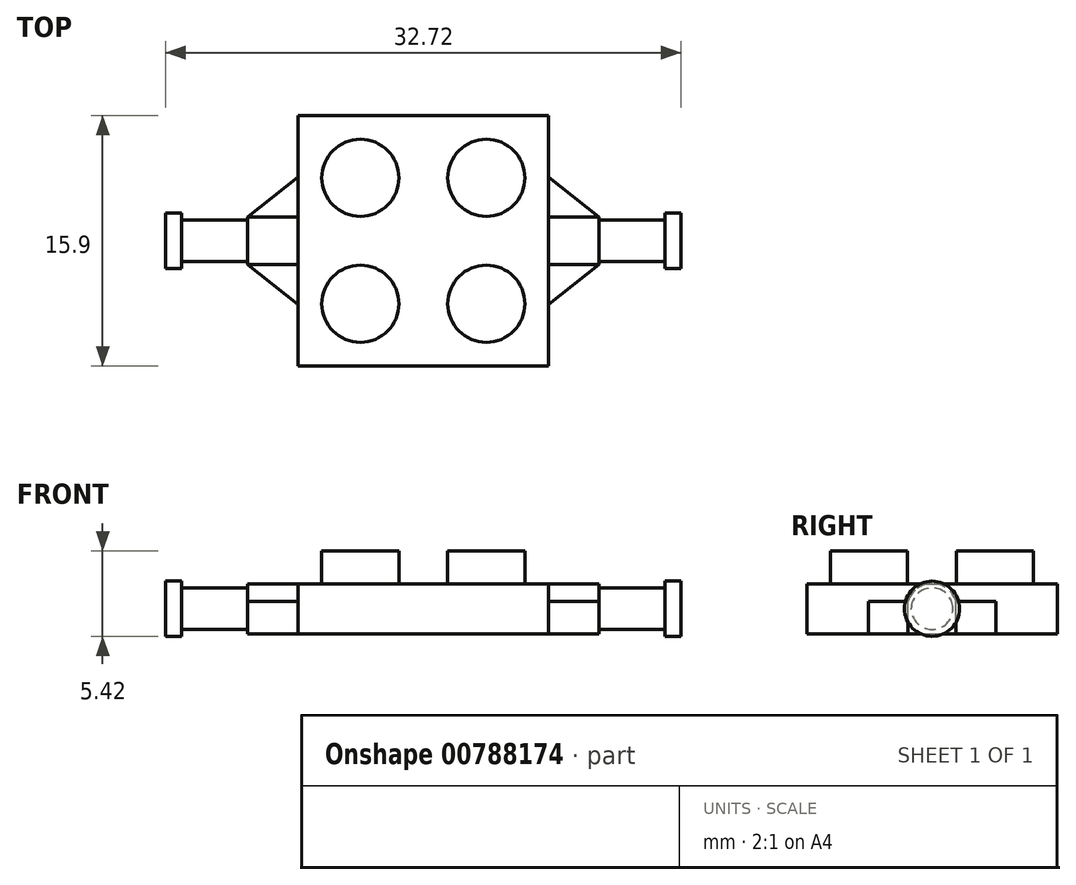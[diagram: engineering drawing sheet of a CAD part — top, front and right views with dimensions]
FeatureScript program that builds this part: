
annotation { "Feature Type Name" : "Feature", "Feature Type Description" : "" }
export const myFeature = defineFeature(function(context is Context, id is Id, definition is map)
    precondition{}
    {
        {
            var Q0;
            Q0=qCreatedBy(makeId("Top.planeOp"),FACE);
            var sketch = newSketch(context, id + "F0", { "sketchPlane" : qUnion([Q0])});
            skLineSegment(sketch, "E0.bottom", {"start": v(0, 0) * mm, "end": v(15.9, 0) * mm});
            skLineSegment(sketch, "E0.top", {"start": v(0, 15.9) * mm, "end": v(15.9, 15.9) * mm});
            skLineSegment(sketch, "E0.left", {"start": v(0, 0) * mm, "end": v(0, 15.9) * mm});
            skLineSegment(sketch, "E0.right", {"start": v(15.9, 0) * mm, "end": v(15.9, 15.9) * mm});
            skSolve(sketch);
        }
        {
            var Q0;
            Q0=qSketchRegion(id+"F0",true);
            extrude(context, id + "F1", {"entities" : qUnion([Q0]), "depth" : 3.18 * mm, "offsetDistance" : 25 * mm});
        }
        {
            var Q0;
            Q0=makeQuery(id+"F1.opExtrude","CAP_FACE",FACE,{"disambiguationData":[OSD([sQuery(id+"F0.wireOp",EDGE,"E0.bottom"),sQuery(id+"F0.wireOp",EDGE,"E0.top"),sQuery(id+"F0.wireOp",EDGE,"E0.left"),sQuery(id+"F0.wireOp",EDGE,"E0.right")])],"isStart":false});
            var sketch = newSketch(context, id + "F2", { "sketchPlane" : qUnion([Q0])});
            skCircle(sketch, "E1", {"center": v(3.95, 11.95) * mm, "radius": 2.45 * mm});
            skCircle(sketch, "E2", {"center": v(3.95, 3.95) * mm, "radius": 2.45 * mm});
            skCircle(sketch, "E3", {"center": v(11.95, 11.95) * mm, "radius": 2.45 * mm});
            skCircle(sketch, "E4", {"center": v(11.95, 3.95) * mm, "radius": 2.45 * mm});
            skSolve(sketch);
        }
        {
            var Q0;
            Q0=qSketchRegion(id+"F2",true);
            extrude(context, id + "F3", {"entities" : qUnion([Q0]), "operationType" : NewBodyOperationType.ADD, "depth" : 2.08 * mm, "offsetDistance" : 25 * mm});
        }
        {
            var Q0;
            Q0=makeQuery(id+"F1.opExtrude","SWEPT_FACE",FACE,{"disambiguationData":[OSD([sQuery(id+"F0.wireOp",EDGE,"E0.right")])]});
            var sketch = newSketch(context, id + "F4", { "sketchPlane" : qUnion([Q0])});
            skCircle(sketch, "E5", {"center": v(7.95, 1.6) * mm, "radius": 1.6 * mm});
            skPoint(sketch, "E5.centerSnap0", {"position": v(15.9, 1.6) * mm});
            skPoint(sketch, "E5.centerSnap1", {"position": v(7.95, 3.18) * mm});
            skLineSegment(sketch, "E6", {"start": v(12, 0) * mm, "end": v(12, 2.05) * mm});
            skLineSegment(sketch, "E7", {"start": v(12, 2.05) * mm, "end": v(9.47, 2.05) * mm});
            skLineSegment(sketch, "E8", {"start": v(3.91, 0) * mm, "end": v(3.91, 2.05) * mm});
            skLineSegment(sketch, "E9", {"start": v(3.91, 2.05) * mm, "end": v(6.43, 2.05) * mm});
            skSolve(sketch);
        }
        {
            var Q0;
            Q0=qSketchRegion(id+"F4",true);
            var Q1;
            {var subQ4=sQuery(id+"F4.wireOp",EDGE,"E8");Q1=makeQuery(id+"F4.imprint","IMPRINT",FACE,{"disambiguationData":[TD([[makeQuery(id+"F4.imprint","IMPRINT",EDGE,{"derivedFrom":subQ4}),-1.0]])]});}
            var Q2;
            {var subQ4=sQuery(id+"F4.wireOp",EDGE,"E6");Q2=makeQuery(id+"F4.imprint","IMPRINT",FACE,{"disambiguationData":[TD([[makeQuery(id+"F4.imprint","IMPRINT",EDGE,{"derivedFrom":subQ4}),1.0]])]});}
            extrude(context, id + "F5", {"entities" : qUnion([Q0, Q1, Q2]), "operationType" : NewBodyOperationType.ADD, "depth" : 3.2 * mm, "offsetDistance" : 25 * mm});
        }
        {
            var Q0;
            Q0=makeQuery(id+"F5.opExtrude","SWEPT_FACE",FACE,{"disambiguationData":[OSD([sQuery(id+"F4.wireOp",EDGE,"E9")])]});
            var sketch = newSketch(context, id + "F6", { "sketchPlane" : qUnion([Q0])});
            skLineSegment(sketch, "E10", {"start": v(19.11, 6.43) * mm, "end": v(15.9, 3.91) * mm});
            skSolve(sketch);
        }
        {
            var Q0;
            Q0=makeQuery(id+"F6.imprint","IMPRINT",FACE,{"disambiguationData":[TD([[makeQuery(id+"F6.imprint","IMPRINT",EDGE,{"derivedFrom":sQuery(id+"F6.wireOp",EDGE,"E10")}),1.0]])]});
            extrude(context, id + "F7", {"entities" : qUnion([Q0]), "operationType" : NewBodyOperationType.REMOVE, "oppositeDirection" : true, "depth" : 4 * mm, "offsetDistance" : 25 * mm});
        }
        {
            var Q0;
            Q0=makeQuery(id+"F5.opExtrude","SWEPT_FACE",FACE,{"disambiguationData":[OSD([sQuery(id+"F4.wireOp",EDGE,"E7")])]});
            var sketch = newSketch(context, id + "F8", { "sketchPlane" : qUnion([Q0])});
            skLineSegment(sketch, "E11", {"start": v(19.11, 9.47) * mm, "end": v(15.9, 12) * mm});
            skSolve(sketch);
        }
        {
            var Q0;
            Q0=makeQuery(id+"F8.imprint","IMPRINT",FACE,{"disambiguationData":[TD([[makeQuery(id+"F8.imprint","IMPRINT",EDGE,{"derivedFrom":sQuery(id+"F8.wireOp",EDGE,"E11")}),-1.0]])]});
            extrude(context, id + "F9", {"entities" : qUnion([Q0]), "operationType" : NewBodyOperationType.REMOVE, "oppositeDirection" : true, "depth" : 4 * mm, "offsetDistance" : 25 * mm});
        }
        {
            var Q0;
            Q0=makeQuery(id+"F5.opExtrude","CAP_FACE",FACE,{"disambiguationData":[OSD([sQuery(id+"F0.wireOp",EDGE,"E0.right"),sQuery(id+"F4.wireOp",EDGE,"E5"),sQuery(id+"F4.wireOp",EDGE,"E6"),sQuery(id+"F4.wireOp",EDGE,"E7"),sQuery(id+"F4.wireOp",EDGE,"E8"),sQuery(id+"F4.wireOp",EDGE,"E9")])],"isStart":false});
            var sketch = newSketch(context, id + "F10", { "sketchPlane" : qUnion([Q0])});
            skCircle(sketch, "E12", {"center": v(7.95, 1.6) * mm, "radius": 1.32 * mm});
            skSolve(sketch);
        }
        {
            var Q0;
            Q0=qSketchRegion(id+"F10",true);
            extrude(context, id + "F11", {"entities" : qUnion([Q0]), "operationType" : NewBodyOperationType.ADD, "depth" : 4.2 * mm, "offsetDistance" : 25 * mm});
        }
        {
            var Q0;
            Q0=makeQuery(id+"F11.opExtrude","CAP_FACE",FACE,{"disambiguationData":[OSD([sQuery(id+"F10.wireOp",EDGE,"E12")])],"isStart":false});
            var sketch = newSketch(context, id + "F12", { "sketchPlane" : qUnion([Q0])});
            skCircle(sketch, "E13", {"center": v(7.95, 1.6) * mm, "radius": 1.75 * mm});
            skSolve(sketch);
        }
        {
            var Q0;
            Q0=qSketchRegion(id+"F12",true);
            extrude(context, id + "F13", {"entities" : qUnion([Q0]), "operationType" : NewBodyOperationType.ADD, "depth" : 1 * mm, "offsetDistance" : 25 * mm});
        }
        {
            var Q0;
            Q0=makeQuery(id+"F1.opExtrude","SWEPT_FACE",FACE,{"disambiguationData":[OSD([sQuery(id+"F0.wireOp",EDGE,"E0.left")])]});
            var sketch = newSketch(context, id + "F14", { "sketchPlane" : qUnion([Q0])});
            skCircle(sketch, "E14", {"center": v(-7.95, 1.6) * mm, "radius": 1.6 * mm});
            skPoint(sketch, "E14.centerSnap0", {"position": v(0, 1.6) * mm});
            skPoint(sketch, "E14.centerSnap1", {"position": v(-7.95, 3.18) * mm});
            skLineSegment(sketch, "E15", {"start": v(-12, 0) * mm, "end": v(-12, 2.05) * mm});
            skLineSegment(sketch, "E16", {"start": v(-12, 2.05) * mm, "end": v(-9.47, 2.05) * mm});
            skLineSegment(sketch, "E17", {"start": v(-3.91, 0) * mm, "end": v(-3.91, 2.05) * mm});
            skLineSegment(sketch, "E18", {"start": v(-3.91, 2.05) * mm, "end": v(-6.43, 2.05) * mm});
            skSolve(sketch);
        }
        {
            var Q0;
            Q0=qSketchRegion(id+"F14",true);
            var Q1;
            {var subQ4=sQuery(id+"F14.wireOp",EDGE,"E15");Q1=makeQuery(id+"F14.imprint","IMPRINT",FACE,{"disambiguationData":[TD([[makeQuery(id+"F14.imprint","IMPRINT",EDGE,{"derivedFrom":subQ4}),-1.0]])]});}
            var Q2;
            {var subQ4=sQuery(id+"F14.wireOp",EDGE,"E17");Q2=makeQuery(id+"F14.imprint","IMPRINT",FACE,{"disambiguationData":[TD([[makeQuery(id+"F14.imprint","IMPRINT",EDGE,{"derivedFrom":subQ4}),1.0]])]});}
            extrude(context, id + "F15", {"entities" : qUnion([Q0, Q1, Q2]), "operationType" : NewBodyOperationType.ADD, "depth" : 3.2 * mm, "offsetDistance" : 25 * mm});
        }
        {
            var Q0;
            Q0=makeQuery(id+"F15.opExtrude","CAP_FACE",FACE,{"disambiguationData":[OSD([sQuery(id+"F0.wireOp",EDGE,"E0.left"),sQuery(id+"F14.wireOp",EDGE,"E14"),sQuery(id+"F14.wireOp",EDGE,"E15"),sQuery(id+"F14.wireOp",EDGE,"E16"),sQuery(id+"F14.wireOp",EDGE,"E17"),sQuery(id+"F14.wireOp",EDGE,"E18")])],"isStart":false});
            var sketch = newSketch(context, id + "F16", { "sketchPlane" : qUnion([Q0])});
            skCircle(sketch, "E19", {"center": v(-7.95, 1.6) * mm, "radius": 1.32 * mm});
            skSolve(sketch);
        }
        {
            var Q0;
            Q0=qSketchRegion(id+"F16",true);
            extrude(context, id + "F17", {"entities" : qUnion([Q0]), "operationType" : NewBodyOperationType.ADD, "depth" : 4.2 * mm, "offsetDistance" : 25 * mm});
        }
        {
            var Q0;
            Q0=makeQuery(id+"F17.opExtrude","CAP_FACE",FACE,{"disambiguationData":[OSD([sQuery(id+"F16.wireOp",EDGE,"E19")])],"isStart":false});
            var sketch = newSketch(context, id + "F18", { "sketchPlane" : qUnion([Q0])});
            skCircle(sketch, "E20", {"center": v(-7.95, 1.6) * mm, "radius": 1.75 * mm});
            skSolve(sketch);
        }
        {
            var Q0;
            Q0=qSketchRegion(id+"F18",true);
            extrude(context, id + "F19", {"entities" : qUnion([Q0]), "operationType" : NewBodyOperationType.ADD, "depth" : 1 * mm, "offsetDistance" : 25 * mm});
        }
        {
            var Q0;
            Q0=makeQuery(id+"F15.opExtrude","SWEPT_FACE",FACE,{"disambiguationData":[OSD([sQuery(id+"F14.wireOp",EDGE,"E18")])]});
            var sketch = newSketch(context, id + "F20", { "sketchPlane" : qUnion([Q0])});
            skLineSegment(sketch, "E21", {"start": v(-3.21, 6.43) * mm, "end": v(0, 3.91) * mm});
            skSolve(sketch);
        }
        {
            var Q0;
            Q0=makeQuery(id+"F20.imprint","IMPRINT",FACE,{"disambiguationData":[TD([[makeQuery(id+"F20.imprint","IMPRINT",EDGE,{"derivedFrom":sQuery(id+"F20.wireOp",EDGE,"E21")}),-1.0]])]});
            extrude(context, id + "F21", {"entities" : qUnion([Q0]), "operationType" : NewBodyOperationType.REMOVE, "oppositeDirection" : true, "depth" : 25 * mm, "offsetDistance" : 25 * mm});
        }
        {
            var Q0;
            Q0=makeQuery(id+"F15.opExtrude","SWEPT_FACE",FACE,{"disambiguationData":[OSD([sQuery(id+"F14.wireOp",EDGE,"E16")])]});
            var sketch = newSketch(context, id + "F22", { "sketchPlane" : qUnion([Q0])});
            skLineSegment(sketch, "E22", {"start": v(-3.21, 9.47) * mm, "end": v(0, 12) * mm});
            skSolve(sketch);
        }
        {
            var Q0;
            Q0=makeQuery(id+"F22.imprint","IMPRINT",FACE,{"disambiguationData":[TD([[makeQuery(id+"F22.imprint","IMPRINT",EDGE,{"derivedFrom":sQuery(id+"F22.wireOp",EDGE,"E22")}),1.0]])]});
            extrude(context, id + "F23", {"entities" : qUnion([Q0]), "operationType" : NewBodyOperationType.REMOVE, "oppositeDirection" : true, "depth" : 25 * mm, "offsetDistance" : 25 * mm});
        }
    });
